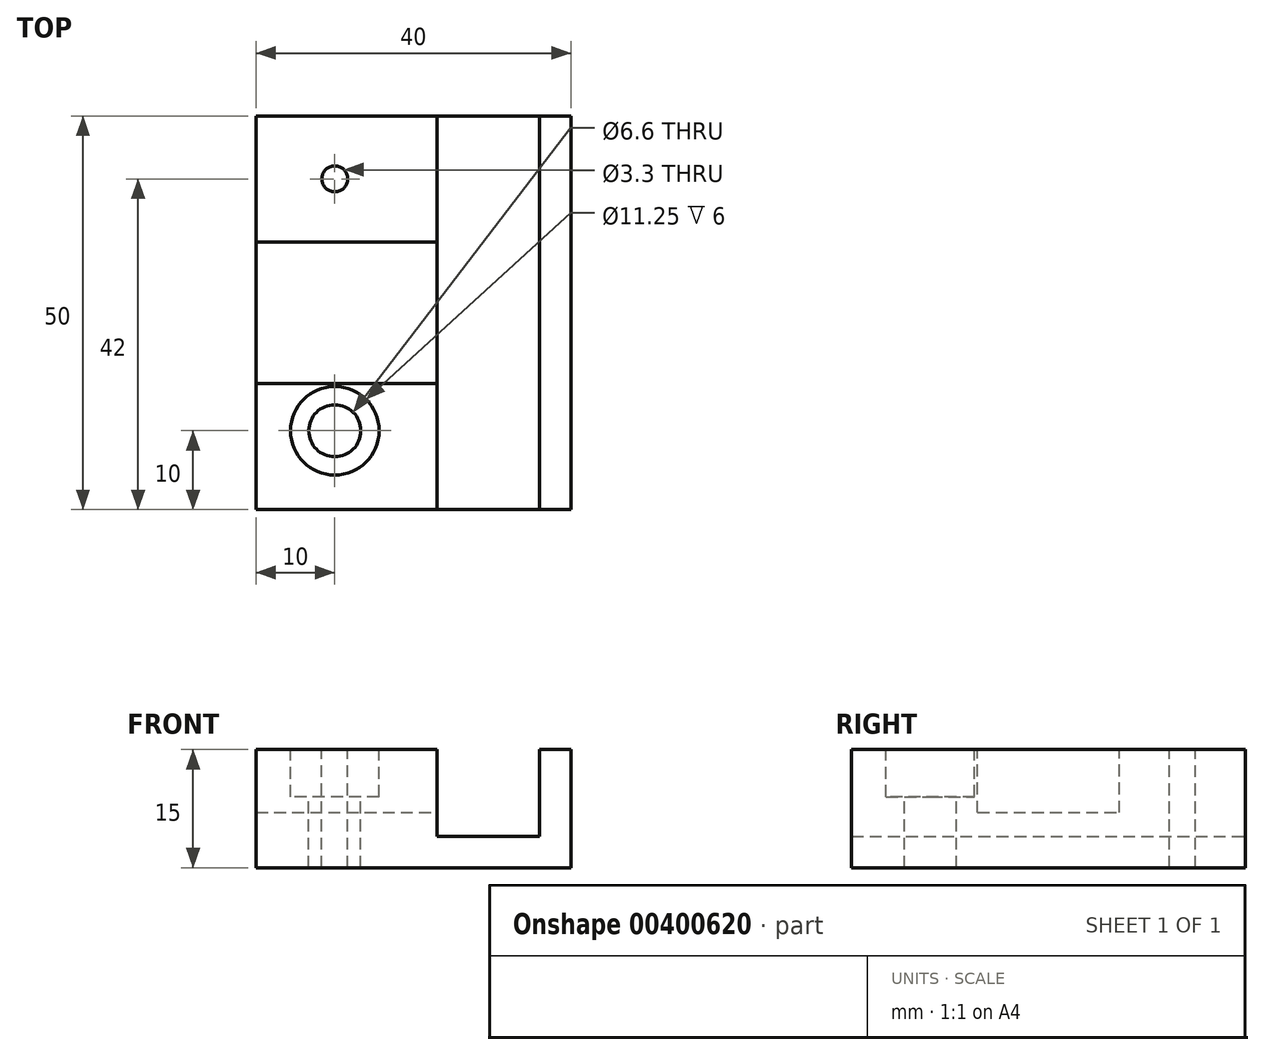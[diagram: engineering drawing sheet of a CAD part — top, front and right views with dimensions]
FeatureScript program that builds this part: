
annotation { "Feature Type Name" : "Feature", "Feature Type Description" : "" }
export const myFeature = defineFeature(function(context is Context, id is Id, definition is map)
    precondition{}
    {
        {
            var Q0;
            Q0=qCreatedBy(makeId("Front.planeOp"),FACE);
            var sketch = newSketch(context, id + "F0", { "sketchPlane" : qUnion([Q0])});
            skLineSegment(sketch, "E0", {"start": v(0, 0) * mm, "end": v(0, -30) * mm});
            skLineSegment(sketch, "E1", {"start": v(0, -30) * mm, "end": v(-40, -30) * mm});
            skLineSegment(sketch, "E2", {"start": v(-40, -30) * mm, "end": v(-40, 0) * mm});
            skLineSegment(sketch, "E3", {"start": v(-17, 0) * mm, "end": v(-17, -11) * mm});
            skLineSegment(sketch, "E4", {"start": v(-17, -11) * mm, "end": v(-4, -11) * mm});
            skLineSegment(sketch, "E5", {"start": v(-4, -11) * mm, "end": v(-4, 0) * mm});
            skLineSegment(sketch, "E6", {"start": v(-4, 0) * mm, "end": v(0, 0) * mm});
            skLineSegment(sketch, "E7", {"start": v(-40, 0) * mm, "end": v(-17, 0) * mm});
            skSolve(sketch);
        }
        {
            var Q0;
            Q0 = qSketchRegion(id + "F0", true);
            var Q1;
            Q1=makeQuery(id+"F0.imprint","IMPRINT",FACE,{"disambiguationData":[TD([[makeQuery(id+"F0.imprint","IMPRINT",EDGE,{"derivedFrom":sQuery(id+"F0.wireOp",EDGE,"E0")}),-1.0]])]});
            extrude(context, id + "F1", {"entities" : qUnion([Q0, Q1]), "depth" : 50 * mm});
        }
        {
            var Q0;
            Q0=makeQuery(id+"F1.opExtrude","SWEPT_FACE",FACE,{"disambiguationData":[OSD([sQuery(id+"F0.wireOp",EDGE,"E7")])]});
            var sketch = newSketch(context, id + "F2", { "sketchPlane" : qUnion([Q0])});
            skLineSegment(sketch, "E8", {"start": v(-40, -25) * mm, "end": v(-40, -16) * mm});
            skLineSegment(sketch, "E9", {"start": v(-40, -16) * mm, "end": v(-17, -16) * mm});
            skLineSegment(sketch, "E10", {"start": v(-40, -25) * mm, "end": v(-40, -34) * mm});
            skLineSegment(sketch, "E11", {"start": v(-40, -34) * mm, "end": v(-17, -34) * mm});
            skLineSegment(sketch, "E12", {"start": v(-17, -34) * mm, "end": v(-17, -16) * mm});
            skSolve(sketch);
        }
        {
            var Q0;
            Q0=makeQuery(id+"F2.imprint","IMPRINT",FACE,{"disambiguationData":[TD([[makeQuery(id+"F2.imprint","IMPRINT",EDGE,{"derivedFrom":sQuery(id+"F2.wireOp",EDGE,"E8")}),-1.0]])]});
            extrude(context, id + "F3", {"entities" : qUnion([Q0]), "operationType" : NewBodyOperationType.REMOVE, "oppositeDirection" : true, "depth" : 8 * mm});
        }
        {
            var Q0;
            {var subQ0=sQuery(id+"F0.wireOp",EDGE,"E7");Q0=makeQuery(id+"F3.boolean.opBoolean","SPLIT",FACE,{"disambiguationData":[TD([makeQuery(id+"F3.opExtrude","SWEPT_FACE",FACE,{"disambiguationData":[OSD([sQuery(id+"F2.wireOp",EDGE,"E11")])]})])],"derivedFrom":makeQuery(id+"F1.opExtrude","SWEPT_FACE",FACE,{"disambiguationData":[OSD([subQ0])]})});}
            var sketch = newSketch(context, id + "F4", { "sketchPlane" : qUnion([Q0])});
            skPoint(sketch, "E13", {"position": v(-30, -40) * mm});
            skSolve(sketch);
        }
        {
            var Q0;
            Q0=sQuery(id+"F4.wireOp",VERTEX,"E13");
            var Q1;
            Q1=makeQuery(id+"F1.opExtrude","SWEPT_BODY",BODY,{"disambiguationData":[OSD([sQuery(id+"F0.wireOp",EDGE,"E0"),sQuery(id+"F0.wireOp",EDGE,"E1"),sQuery(id+"F0.wireOp",EDGE,"E2"),sQuery(id+"F0.wireOp",EDGE,"E3"),sQuery(id+"F0.wireOp",EDGE,"E4"),sQuery(id+"F0.wireOp",EDGE,"E5"),sQuery(id+"F0.wireOp",EDGE,"E6"),sQuery(id+"F0.wireOp",EDGE,"E7")])]});
            hole(context, id + "F5", {"style" : HoleStyle.C_BORE, "endStyle" : HoleEndStyle.THROUGH, "standardTappedOrClearance" : lookupTablePath({ "standard" : "ISO", "fit" : "Normal", "size" : "M6", "type" : "Clearance" }), "standardBlindInLast" : lookupTablePath({ "fit" : "Standard", "standard" : "ISO", "size" : "M6", "type" : "Clearance" }), "holeDiameter" : 6.6 * mm, "cBoreDiameter" : 11.25 * mm, "cBoreDepth" : 6 * mm, "isTappedThrough" : true, "tappedDepth" : 50 * mm, "tapClearance" : 3, "startFromSketch" : true, "locations" : qUnion([Q0]), "scope" : qUnion([Q1])});
        }
        {
            var Q0;
            Q0=qCreatedBy(makeId("Top.planeOp"),FACE);
            var sketch = newSketch(context, id + "F6", { "sketchPlane" : qUnion([Q0])});
            skPoint(sketch, "E14", {"position": v(-30, -8) * mm});
            skSolve(sketch);
        }
        {
            var Q0;
            Q0=sQuery(id+"F6.wireOp",VERTEX,"E14");
            var Q1;
            Q1=makeQuery(id+"F1.opExtrude","SWEPT_BODY",BODY,{"disambiguationData":[OSD([sQuery(id+"F0.wireOp",EDGE,"E0"),sQuery(id+"F0.wireOp",EDGE,"E1"),sQuery(id+"F0.wireOp",EDGE,"E2"),sQuery(id+"F0.wireOp",EDGE,"E3"),sQuery(id+"F0.wireOp",EDGE,"E4"),sQuery(id+"F0.wireOp",EDGE,"E5"),sQuery(id+"F0.wireOp",EDGE,"E6"),sQuery(id+"F0.wireOp",EDGE,"E7")])]});
            hole(context, id + "F7", {"style" : HoleStyle.SIMPLE, "endStyle" : HoleEndStyle.THROUGH, "standardTappedOrClearance" : lookupTablePath({ "standard" : "ISO", "fit" : "Normal", "size" : "M3", "type" : "Clearance" }), "standardBlindInLast" : lookupTablePath({ "fit" : "Standard", "standard" : "ISO", "size" : "M3", "type" : "Clearance" }), "holeDiameter" : 3.3 * mm, "isTappedThrough" : true, "tappedDepth" : 50 * mm, "tapClearance" : 3, "startFromSketch" : true, "locations" : qUnion([Q0]), "scope" : qUnion([Q1])});
        }
        {
            var Q0;
            Q0=makeQuery(id+"F1.opExtrude","SWEPT_FACE",FACE,{"disambiguationData":[OSD([sQuery(id+"F0.wireOp",EDGE,"E1")])]});
            extrude(context, id + "F8", {"entities" : qUnion([Q0]), "operationType" : NewBodyOperationType.REMOVE, "oppositeDirection" : true, "depth" : 15 * mm, "offsetDistance" : 25 * mm});
        }
    });
